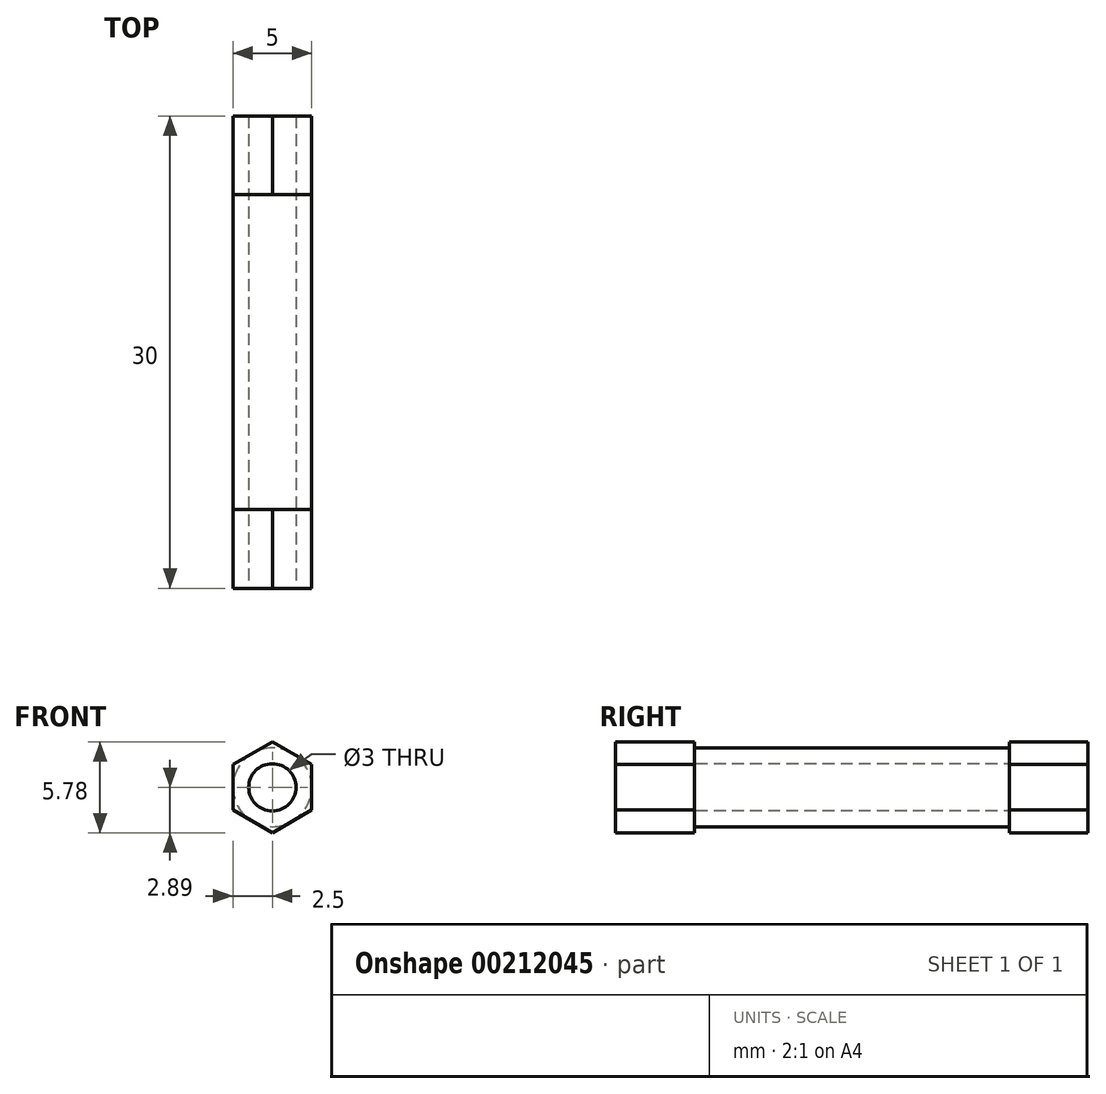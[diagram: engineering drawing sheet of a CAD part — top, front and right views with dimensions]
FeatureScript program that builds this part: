
annotation { "Feature Type Name" : "Feature", "Feature Type Description" : "" }
export const myFeature = defineFeature(function(context is Context, id is Id, definition is map)
    precondition{}
    {
        {
            assignVariable(context, id + "F0", {"name" : "StandoffHeight", "anyValue" : 30});
        }
        {
            var Q0;
            Q0=qCreatedBy(makeId("Front.planeOp"),FACE);
            var sketch = newSketch(context, id + "F1", { "sketchPlane" : qUnion([Q0])});
            skCircle(sketch, "E0", {"center": v(0, 0) * mm, "radius": 2.5 * mm});
            skCircle(sketch, "E1.cCircle", {"center": v(0, 0) * mm, "radius": 2.5 * mm, "construction": true});
            skPoint(sketch, "E1.0.midPoint", {"position": v(-1.25, 2.17) * mm});
            skSolve(sketch);
        }
        {
            var Q0;
            Q0=makeQuery(id+"F1.imprint","IMPRINT",FACE,{"disambiguationData":[TD([[makeQuery(id+"F1.imprint","IMPRINT",EDGE,{"derivedFrom":sQuery(id+"F1.wireOp",EDGE,"E0")}),1.0]])]});
            var Q1;
            Q1 = qSketchRegion(id + "F3", true);
            extrude(context, id + "F2", {"entities" : qUnion([Q0, Q1]), "depth" : (getVariable(context, 'StandoffHeight') / 2 - 5) * mm});
        }
        {
            var Q0;
            Q0=makeQuery(id+"F2.opExtrude","CAP_FACE",FACE,{"disambiguationData":[OSD([sQuery(id+"F1.wireOp",EDGE,"E0")])],"isStart":false});
            var sketch = newSketch(context, id + "F3", { "sketchPlane" : qUnion([Q0])});
            skCircle(sketch, "E2.cCircle", {"center": v(0, 0) * mm, "radius": 2.5 * mm, "construction": true});
            skLineSegment(sketch, "E2.0", {"start": v(-2.5, -1.44) * mm, "end": v(-2.5, 1.44) * mm});
            skLineSegment(sketch, "E2.1", {"start": v(-2.5, 1.44) * mm, "end": v(0, 2.89) * mm});
            skLineSegment(sketch, "E2.2", {"start": v(0, 2.89) * mm, "end": v(2.5, 1.44) * mm});
            skLineSegment(sketch, "E2.3", {"start": v(2.5, 1.44) * mm, "end": v(2.5, -1.44) * mm});
            skLineSegment(sketch, "E2.4", {"start": v(2.5, -1.44) * mm, "end": v(0, -2.89) * mm});
            skLineSegment(sketch, "E2.5", {"start": v(0, -2.89) * mm, "end": v(-2.5, -1.44) * mm});
            skPoint(sketch, "E2.0.midPoint", {"position": v(-2.5, 0) * mm});
            skSolve(sketch);
        }
        {
            var Q0;
            Q0 = qSketchRegion(id + "F3", true);
            extrude(context, id + "F4", {"entities" : qUnion([Q0]), "operationType" : NewBodyOperationType.ADD, "depth" : 5 * mm});
        }
        {
            var Q0;
            Q0=sQuery(id+"F1.wireOp",VERTEX,"E0.center");
            var Q1;
            Q1=makeQuery(id+"F2.opExtrude","SWEPT_BODY",BODY,{"disambiguationData":[OSD([sQuery(id+"F1.wireOp",EDGE,"E0")])]});
            hole(context, id + "F5", {"style" : HoleStyle.SIMPLE, "endStyle" : HoleEndStyle.THROUGH, "oppositeDirection" : true, "holeDiameter" : 3 * mm, "locations" : qUnion([Q0]), "scope" : qUnion([Q1]), "isTappedThrough" : true, "startStyle" : HoleStartStyle.PART});
        }
        {
            var Q0;
            Q0=makeQuery(id+"F2.opExtrude","SWEPT_BODY",BODY,{"disambiguationData":[OSD([sQuery(id+"F1.wireOp",EDGE,"E0")])]});
            var Q1;
            Q1=makeQuery(id+"F1.imprint","IMPRINT",FACE,{"disambiguationData":[TD([[makeQuery(id+"F1.imprint","IMPRINT",EDGE,{"derivedFrom":sQuery(id+"F1.wireOp",EDGE,"E0")}),1.0]])]});
            mirror(context, id + "F6", {"operationType" : NewBodyOperationType.ADD, "entities" : qUnion([Q0]), "mirrorPlane" : qUnion([Q1])});
        }
    });
